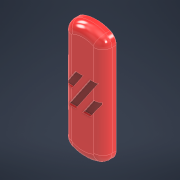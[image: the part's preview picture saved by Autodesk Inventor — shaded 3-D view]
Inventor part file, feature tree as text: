
AUTODESK INVENTOR PART (.ipt)
format: ipt  version: 2022.1 (Build 261234000, 234)  size: 317,952 bytes
history: native  units: mm
features: sketch x8, extrude x7, projected_geometry x6, direct_edit x5, move_body x5, reference x4, other x3, hole x2, chamfer x2, fillet x1, plane x1
ambient origin geometry x8: Origin, YZ Plane, XZ Plane, XY Plane, X Axis, Y Axis, Z Axis, Center Point
bodies: Volumenkörper1 (feature_tree)
feature tree (44):
  extrude  "Extrusion1"  Depth=4.0mm TaperAngle=0.0deg
  extrude  "Extrusion2"  Depth=3.2mm
  hole  "Bohrung1"  [1 undecoded]
  sketch  "Skizze4"  dims[d109=2.156321mm d110=2.156321mm]
  direct_edit  "Direktbearbeitung1"
  fillet  "Rundung2"  Radius=12.398846mm
  extrude  "Extrusion4"  Depth=2.156321mm
  extrude  "Extrusion5"  Depth=2.479769mm
  extrude  "Extrusion6"  Depth=6.199423mm
  direct_edit  "Direktbearbeitung2"
  direct_edit  "Direktbearbeitung4"
  direct_edit  "Direktbearbeitung5"
  chamfer  "Fase11"  Distance=15.5mm
  plane  "Arbeitsebene1"
  extrude  "Extrusion7"  Depth=0.2mm
  direct_edit  "Direktbearbeitung6"
  hole  "Bohrung2"  [1 undecoded]
  chamfer  "Fase12"  Distance=3.5mm
  extrude  "Extrusion8"  Depth=0.8mm TaperAngle=0.0deg
  sketch  "Skizze1"  dims[d0=4.0mm d1=0.0mm d3=3.1mm d4=0.0mm]
  reference  "Referenz1"
  sketch  "Skizze2"  dims[d5=5.6mm d6=6.0mm d7=7.1mm d8=1.2mm d9=90.0deg d10=3.2mm d11=0.0mm d89=5.6mm]
  reference  "Referenz2"
  sketch  "Skizze3"  dims[d104=5.6mm d107=14.217391mm d108=12.398846mm]
  reference  "Referenz3"
  projected_geometry  "Projizierte Kontur1"
  sketch  "Skizze5"  dims[d111=2.479769mm d112=2.479769mm]
  reference  "Referenz4"
  sketch  "Skizze6"  dims[d113=2.479769mm d114=6.199423mm]
  projected_geometry  "Projizierte Kontur2"
  projected_geometry  "Projizierte Kontur3"
  sketch  "Skizze7"  dims[d115=6.199423mm]
  projected_geometry  "Projizierte Kontur4"
  sketch  "Skizze8"  dims[d116=6.199423mm d117=15.5mm d118=0.641304mm d121=0.0mm d122=0.0mm d123=0.5mm d124=3.5mm d125=0.8mm d126=0.0mm d127=0.0mm d128=0.0mm d129=1.4mm d130=0.0mm d149=0.0mm d150=0.0mm d151=1.0mm d155=0.0mm d156=0.0mm d157=1.5mm d170=0.0mm d171=0.0mm d172=1.0mm d173=0.4mm d174=2.0mm d175=45.0deg d176=4.8mm d177=4.8mm d178=0.0mm d179=0.0mm d180=0.0mm d181=0.0mm d182=0.75mm d183=6.5mm d184=6.0mm d185=7.5mm d186=1.4mm d187=90.0deg d188=4.0mm d189=0.0mm d190=0.5mm d191=2.0mm d192=45.0deg d193=0.2mm d194=0.0mm]
  projected_geometry  "Projizierte Kontur5"
  projected_geometry  "Projizierte Kontur6"
  other  "<userpath>\Desktop\Voron-2-2.4r1\Custom\Front_Idlers\Baugruppe1.iam"
  other  "Baugruppe1.iam"
  other  "Cover1:1"
  move_body  "Verschieben1"
  move_body  "Verschieben2"
  move_body  "Verschieben4"
  move_body  "Verschieben5"
  move_body  "Verschieben6"
note: 2 required parameter values undecoded (feature->parameter linkage not recoverable at this tier; creation-order binding heuristic only, values carry confidence <= 0.55)
